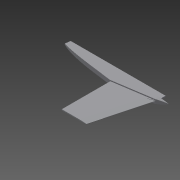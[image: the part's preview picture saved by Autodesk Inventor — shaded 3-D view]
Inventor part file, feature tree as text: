
AUTODESK INVENTOR PART (.ipt)
format: ipt  version: 2014 SP1 (Build 180222100, 222)  size: 157,696 bytes
history: native  units: mm
features: sketch x4, extrude x4, chamfer x2, fillet x1, plane x1
ambient origin geometry x8: Origin, YZ Plane, XZ Plane, XY Plane, X Axis, Y Axis, Z Axis, Center Point
bodies: Solid1 (feature_tree)
feature tree (12):
  sketch  "Sketch1"  dims[d5=25.0mm d6=5.0mm d7=0.0mm d21=120.0mm]
  extrude  "Extrusion1"  Depth=5.0mm TaperAngle=0.0deg
  fillet  "Fillet4"  Radius=120.0mm
  chamfer  "Chamfer3"  Distance=30.0mm
  chamfer  "Chamfer4"  Distance=30.0mm
  extrude  "Extrusion2"  TaperAngle=0.0deg  [1 undecoded]
  plane  "Work Plane1"
  sketch  "Sketch2"  dims[d22=40.0mm]
  extrude  "Extrusion3"  Depth=700.0mm TaperAngle=0.0deg
  extrude  "Extrusion4"  Depth=700.0mm TaperAngle=0.0deg
  sketch  "Sketch3"  dims[d31=2.5mm d32=30.0mm d33=2.0mm d34=0.698132mm d35=30.0mm d36=2.0mm d37=0.698132mm]
  sketch  "Sketch4"  dims[d38=20.0mm d39=0.0mm d40=0.0mm d41=700.0mm d42=0.0mm d43=700.0mm d44=0.0mm]
note: 1 required parameter value undecoded (feature->parameter linkage not recoverable at this tier; creation-order binding heuristic only, values carry confidence <= 0.55)
